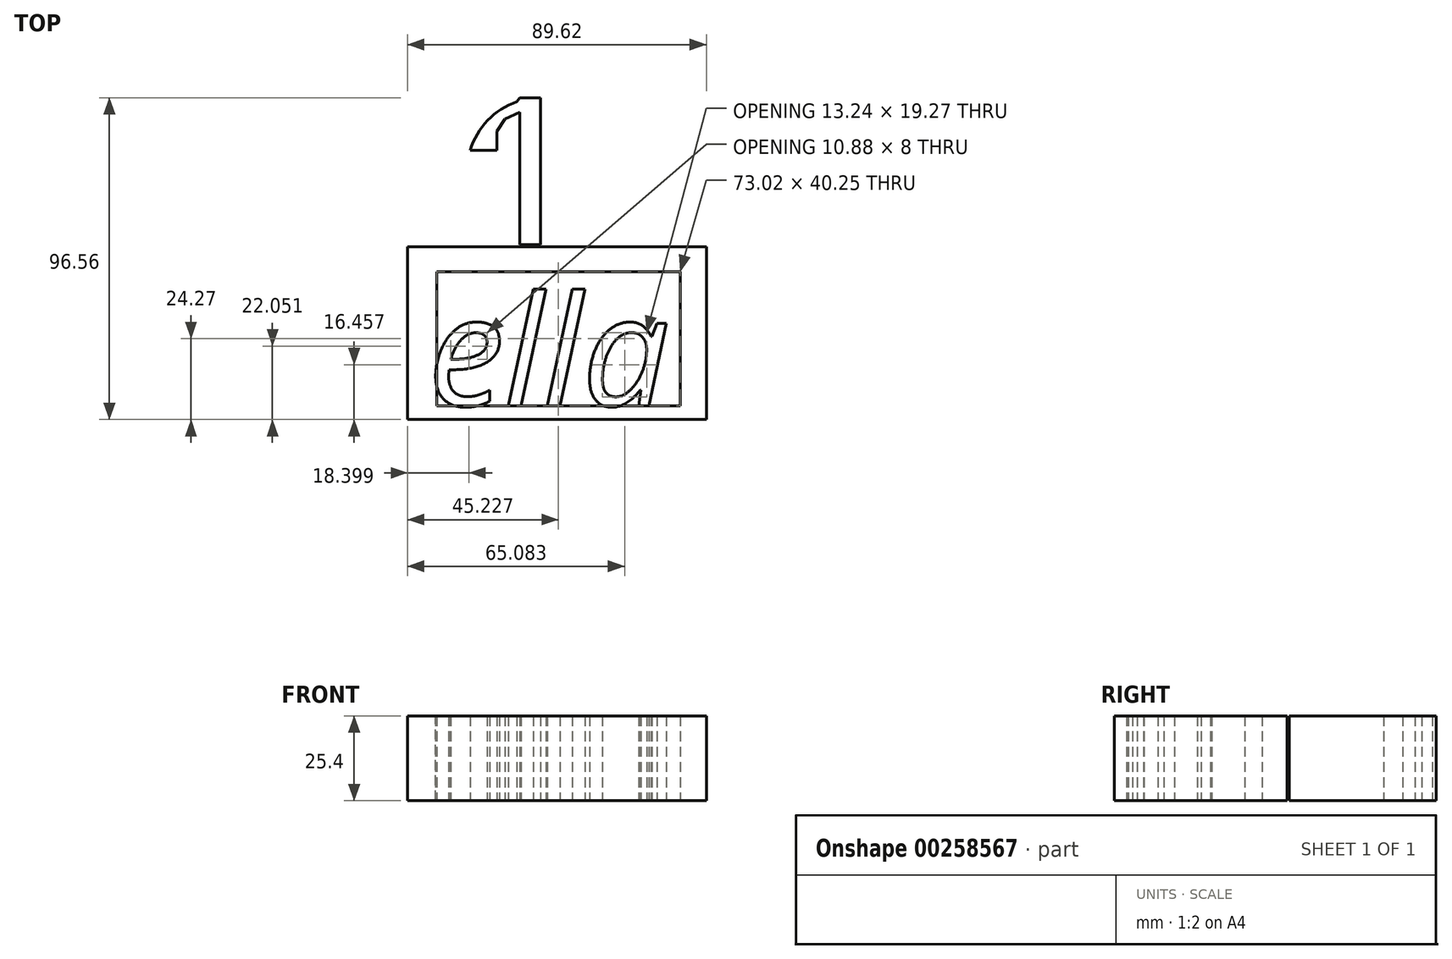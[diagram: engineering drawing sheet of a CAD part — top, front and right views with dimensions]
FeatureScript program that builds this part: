
annotation { "Feature Type Name" : "Feature", "Feature Type Description" : "" }
export const myFeature = defineFeature(function(context is Context, id is Id, definition is map)
    precondition{}
    {
        {
            var Q0;
            Q0=qCreatedBy(makeId("Top.planeOp"),FACE);
            var sketch = newSketch(context, id + "F0", { "sketchPlane" : qUnion([Q0])});
            skText(sketch, "E0", { "text": "ella", "fontName": "OpenSans-Italic.ttf"});
            const initialGuessF0  = {"E0": [-0.07551, -0.0332, 1, 0, 0.0332]};
            skSetInitialGuess(sketch, initialGuessF0);
            skSolve(sketch);
        }
        {
            var Q0;
            Q0=qCreatedBy(makeId("Top.planeOp"),FACE);
            var sketch = newSketch(context, id + "F1", { "sketchPlane" : qUnion([Q0])});
            skLineSegment(sketch, "E1.bottom", {"start": v(-75.1, -33.2) * mm, "end": v(0, -33.2) * mm});
            skLineSegment(sketch, "E1.top", {"start": v(-75.1, -37.34) * mm, "end": v(0, -37.34) * mm});
            skLineSegment(sketch, "E1.left", {"start": v(-75.1, -33.2) * mm, "end": v(-75.1, -37.34) * mm});
            skLineSegment(sketch, "E1.right", {"start": v(0, -33.2) * mm, "end": v(0, -37.34) * mm});
            skLineSegment(sketch, "E2.bottom", {"start": v(0, -37.34) * mm, "end": v(7.88, -37.34) * mm});
            skLineSegment(sketch, "E2.top", {"start": v(0, 7.05) * mm, "end": v(7.88, 7.05) * mm});
            skLineSegment(sketch, "E2.left", {"start": v(0, -37.34) * mm, "end": v(0, 7.05) * mm});
            skLineSegment(sketch, "E2.right", {"start": v(7.88, -37.34) * mm, "end": v(7.88, 7.05) * mm});
            skLineSegment(sketch, "E3.bottom", {"start": v(7.88, 7.05) * mm, "end": v(-73.02, 7.05) * mm});
            skLineSegment(sketch, "E3.top", {"start": v(7.88, 14.52) * mm, "end": v(-73.02, 14.52) * mm});
            skLineSegment(sketch, "E3.left", {"start": v(7.88, 7.05) * mm, "end": v(7.88, 14.52) * mm});
            skLineSegment(sketch, "E3.right", {"start": v(-73.02, 7.05) * mm, "end": v(-73.02, 14.52) * mm});
            skLineSegment(sketch, "E4.bottom", {"start": v(-73.02, 14.52) * mm, "end": v(-81.74, 14.52) * mm});
            skLineSegment(sketch, "E4.top", {"start": v(-73.02, -37.34) * mm, "end": v(-81.74, -37.34) * mm});
            skLineSegment(sketch, "E4.left", {"start": v(-73.02, 14.52) * mm, "end": v(-73.02, -37.34) * mm});
            skLineSegment(sketch, "E4.right", {"start": v(-81.74, 14.52) * mm, "end": v(-81.74, -37.34) * mm});
            skSolve(sketch);
        }
        {
            var Q0;
            {var subQ5=sQuery(id+"F1.wireOp",EDGE,"E3.top");Q0=makeQuery(id+"F1.imprint","IMPRINT",FACE,{"disambiguationData":[TD([[makeQuery(id+"F1.imprint","IMPRINT",EDGE,{"derivedFrom":subQ5}),1.0]])]});}
            var Q1;
            {var subQ3=sQuery(id+"F1.wireOp",EDGE,"E2.bottom");Q1=makeQuery(id+"F1.imprint","IMPRINT",FACE,{"disambiguationData":[TD([[makeQuery(id+"F1.imprint","IMPRINT",EDGE,{"derivedFrom":subQ3}),1.0]])]});}
            var Q2;
            Q2 = qSketchRegion(id + "F0", true);
            var Q3;
            {var subQ5=sQuery(id+"F1.wireOp",EDGE,"E1.top");Q3=makeQuery(id+"F1.imprint","IMPRINT",FACE,{"disambiguationData":[TD([[makeQuery(id+"F1.imprint","IMPRINT",EDGE,{"derivedFrom":subQ5}),1.0]])]});}
            var Q4;
            Q4 = qSketchRegion(id + "F1", true);
            extrude(context, id + "F2", {"entities" : qUnion([Q0, Q1, Q2, Q3, Q4]), "depth" : 25.4 * mm});
        }
        {
            var Q0;
            Q0=qCreatedBy(makeId("Top.planeOp"),FACE);
            var sketch = newSketch(context, id + "F3", { "sketchPlane" : qUnion([Q0])});
            skLineSegment(sketch, "E5.bottom", {"start": v(-48.13, 15.12) * mm, "end": v(-41.83, 15.12) * mm});
            skLineSegment(sketch, "E5.top", {"start": v(-48.13, 59.22) * mm, "end": v(-41.83, 59.22) * mm});
            skLineSegment(sketch, "E5.left", {"start": v(-48.13, 15.12) * mm, "end": v(-48.13, 59.22) * mm});
            skLineSegment(sketch, "E5.right", {"start": v(-41.83, 15.12) * mm, "end": v(-41.83, 59.22) * mm});
            skArc(sketch, "E6", {"start": v(-41.83, 59.22) * mm, "mid": v(-55, 54.86) * mm, "end": v(-62.95, 43.5) * mm});
            skLineSegment(sketch, "E7", {"start": v(-62.95, 43.5) * mm, "end": v(-55, 43.5) * mm});
            skPoint(sketch, "E7.endSnap0", {"position": v(-55, 54.86) * mm});
            skLineSegment(sketch, "E8", {"start": v(-55, 43.5) * mm, "end": v(-55, 54.86) * mm});
            skLineSegment(sketch, "E9", {"start": v(-55, 54.86) * mm, "end": v(-48.13, 54.86) * mm});
            skLineSegment(sketch, "E10", {"start": v(-48.13, 54.86) * mm, "end": v(-60.32, 49.18) * mm});
            skPoint(sketch, "E10.endSnap0", {"position": v(-55, 49.18) * mm});
            skLineSegment(sketch, "E11", {"start": v(-55, 49.18) * mm, "end": v(-48.13, 59.22) * mm});
            skSolve(sketch);
        }
        {
            var Q0;
            Q0 = qSketchRegion(id + "F3", true);
            extrude(context, id + "F4", {"entities" : qUnion([Q0]), "depth" : 25.4 * mm});
        }
    });
